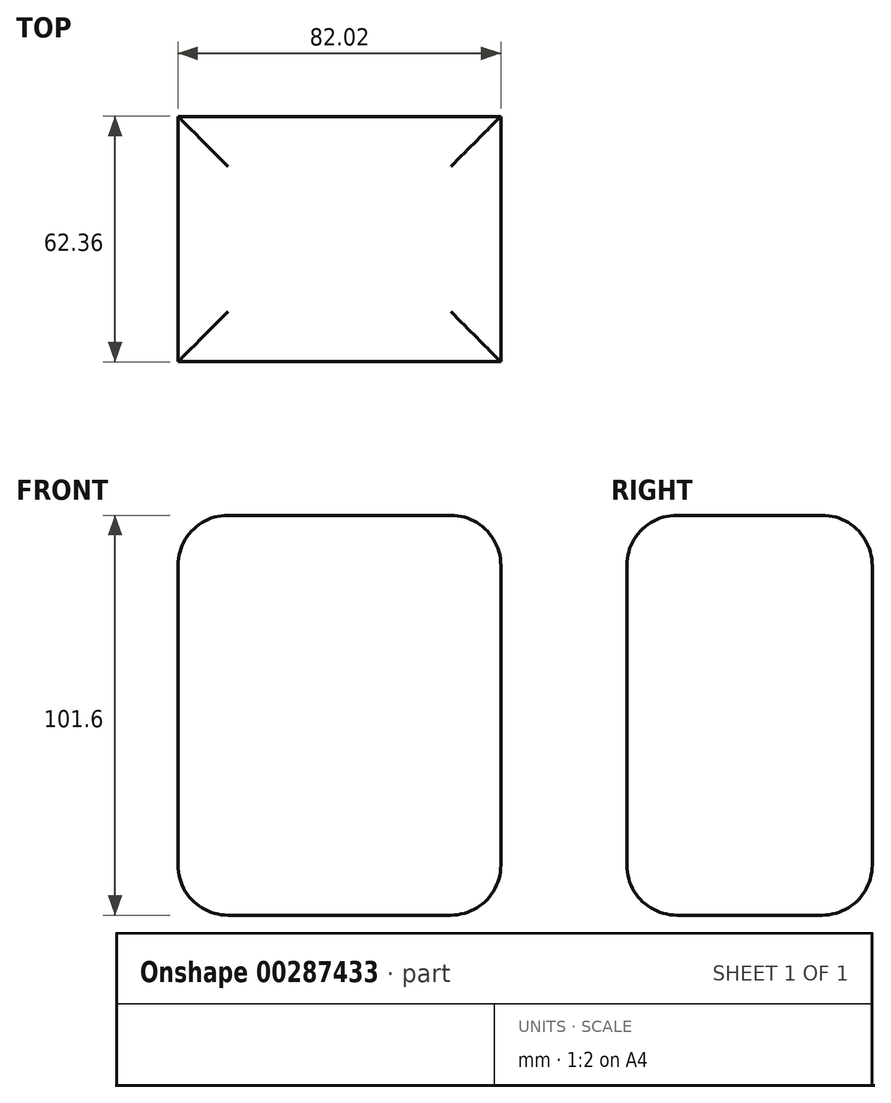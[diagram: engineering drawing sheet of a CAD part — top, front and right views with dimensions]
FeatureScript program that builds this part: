
annotation { "Feature Type Name" : "Feature", "Feature Type Description" : "" }
export const myFeature = defineFeature(function(context is Context, id is Id, definition is map)
    precondition{}
    {
        {
            var Q0;
            Q0=qCreatedBy(makeId("Top.planeOp"),FACE);
            var sketch = newSketch(context, id + "F0", { "sketchPlane" : qUnion([Q0])});
            skLineSegment(sketch, "E0.bottom", {"start": v(41.01, 31.18) * mm, "end": v(-41.01, 31.18) * mm});
            skLineSegment(sketch, "E0.top", {"start": v(41.01, -31.18) * mm, "end": v(-41.01, -31.18) * mm});
            skLineSegment(sketch, "E0.left", {"start": v(41.01, 31.18) * mm, "end": v(41.01, -31.18) * mm});
            skLineSegment(sketch, "E0.right", {"start": v(-41.01, 31.18) * mm, "end": v(-41.01, -31.18) * mm});
            skPoint(sketch, "E0.middle", {"position": v(0, 0) * mm});
            skSolve(sketch);
        }
        {
            var Q0;
            Q0 = qSketchRegion(id + "F0", true);
            extrude(context, id + "F1", {"entities" : qUnion([Q0]), "depth" : 50.8 * mm});
        }
        {
            var Q0;
            Q0=makeQuery(id+"F1.opExtrude","CAP_FACE",FACE,{"disambiguationData":[OSD([sQuery(id+"F0.wireOp",EDGE,"E0.bottom"),sQuery(id+"F0.wireOp",EDGE,"E0.top"),sQuery(id+"F0.wireOp",EDGE,"E0.left"),sQuery(id+"F0.wireOp",EDGE,"E0.right")])],"isStart":false});
            fillet(context, id + "F2", {"entities" : qUnion([Q0]), "radius" : 12.7 * mm, "tangentPropagation" : true, "allowEdgeOverflow" : false});
        }
        {
            var Q0;
            Q0=makeQuery(id+"F1.opExtrude","SWEPT_BODY",BODY,{"disambiguationData":[OSD([sQuery(id+"F0.wireOp",EDGE,"E0.bottom"),sQuery(id+"F0.wireOp",EDGE,"E0.top"),sQuery(id+"F0.wireOp",EDGE,"E0.left"),sQuery(id+"F0.wireOp",EDGE,"E0.right")])]});
            var Q1;
            Q1=qCreatedBy(makeId("Top.planeOp"),FACE);
            mirror(context, id + "F3", {"operationType" : NewBodyOperationType.ADD, "entities" : qUnion([Q0]), "mirrorPlane" : qUnion([Q1])});
        }
    });
